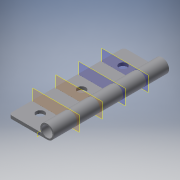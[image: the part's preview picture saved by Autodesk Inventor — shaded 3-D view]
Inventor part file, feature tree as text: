
AUTODESK INVENTOR PART (.ipt)
format: ipt  version: 2019 (Build 230136000, 136)  size: 214,016 bytes
history: native  units: mm
features: other x18, extrude x2, sketch x2, projected_geometry x2, fillet x1
ambient origin geometry x8: Origin, YZ Plane, XZ Plane, XY Plane, X Axis, Y Axis, Z Axis, Center Point
bodies: Body1 (feature_tree), Body2 (feature_tree), Body3 (feature_tree), Body4 (feature_tree), Body5 (feature_tree)
feature tree (25):
  other  "솔리드1"
  extrude  "돌출1"  Depth=25.0mm
  fillet  "모깎기1"  Radius=2.0mm
  extrude  "돌출2"  Depth=9.0mm
  other  "작업 평면1"
  other  "작업 평면3"
  other  "작업 평면4"
  other  "작업 평면5"
  other  "분할1"
  other  "분할3"
  other  "분할4"
  other  "분할5"
  sketch  "스케치1"
  sketch  "스케치2"
  projected_geometry  "투영된 루프1"
  projected_geometry  "투영된 루프2"
  other  "작업 평면2"
  other  "솔리드2"
  other  "솔리드3"
  other  "솔리드6"
  other  "솔리드7"
  other  "솔리드8"
  other  "솔리드9"
  other  "솔리드10"
  other  "솔리드11"
